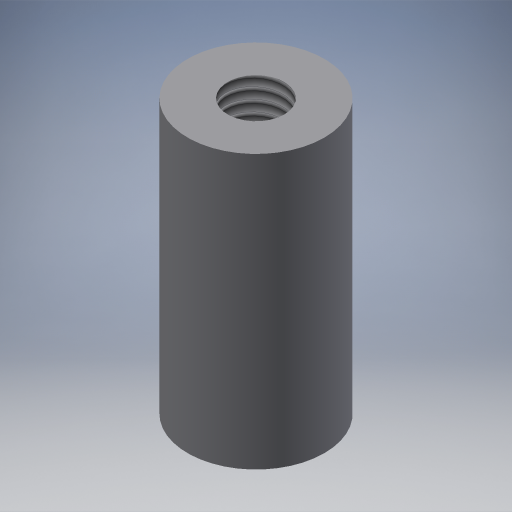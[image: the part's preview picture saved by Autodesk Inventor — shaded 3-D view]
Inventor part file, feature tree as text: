
AUTODESK INVENTOR PART (.ipt)
format: ipt  version: 2024.3 (Build 283343000, 343)  size: 230,912 bytes
history: native  units: mm
features: extrude x1, hole x1, sketch x1
ambient origin geometry x8: Origin, YZ Plane, XZ Plane, XY Plane, X Axis, Y Axis, Z Axis, Center Point
bodies: Volumenkörper1 (feature_tree)
feature tree (3):
  extrude  "Extrusion1"  Depth=20.0mm TaperAngle=0.0deg
  hole  "Bohrung1"  [1 undecoded]
  sketch  "Skizze2"  dims[d0=10.0mm d1=20.0mm d2=0.0mm d3=4.134mm d4=10.0mm d5=4.0mm d6=2.0mm d7=90.0deg d8=8.0mm d9=20.594885mm]
note: 1 required parameter value undecoded (feature->parameter linkage not recoverable at this tier; creation-order binding heuristic only, values carry confidence <= 0.55)
